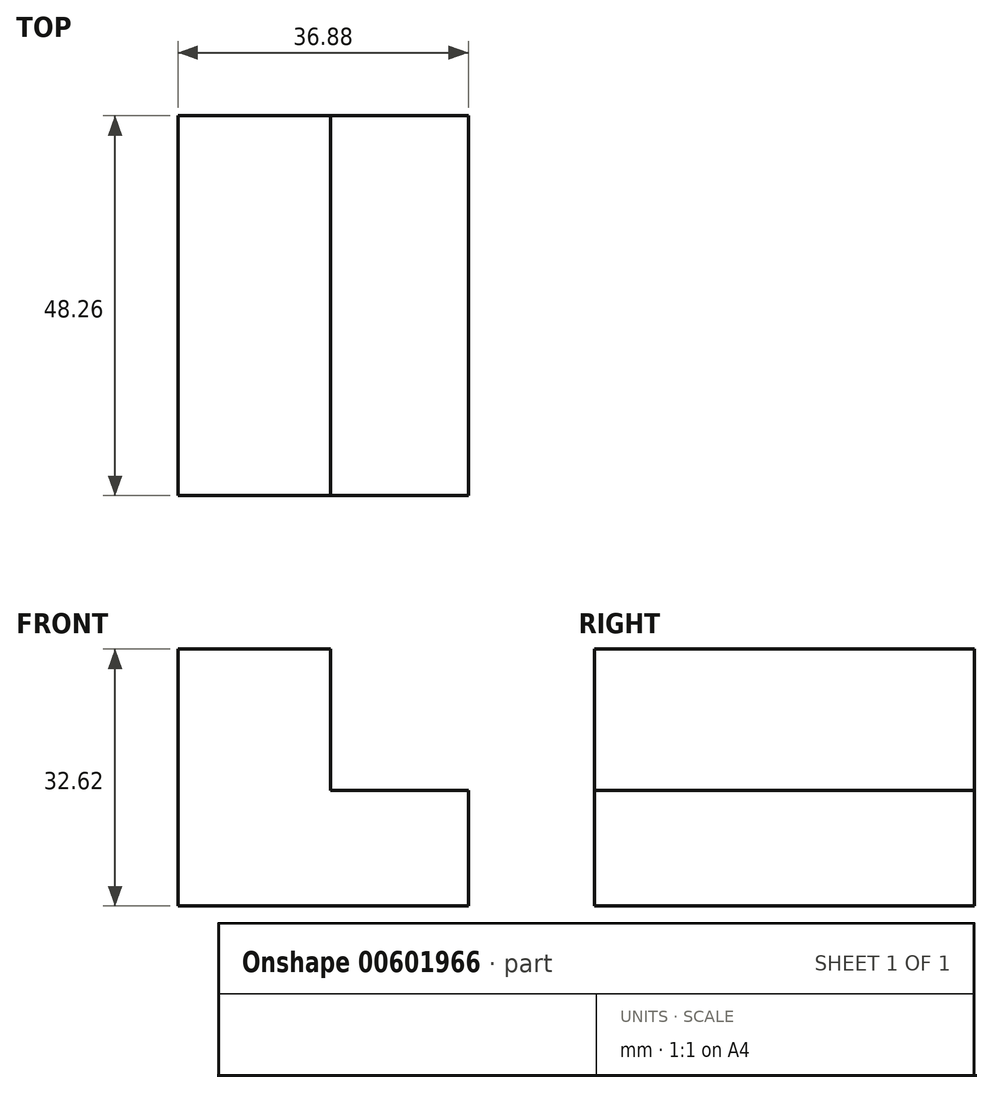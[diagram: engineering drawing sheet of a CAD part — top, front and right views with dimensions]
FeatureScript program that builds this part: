
annotation { "Feature Type Name" : "Feature", "Feature Type Description" : "" }
export const myFeature = defineFeature(function(context is Context, id is Id, definition is map)
    precondition{}
    {
        {
            var Q0;
            Q0=qCreatedBy(makeId("Front.planeOp"),FACE);
            var sketch = newSketch(context, id + "F0", { "sketchPlane" : qUnion([Q0])});
            skLineSegment(sketch, "E0", {"start": v(-19.35, 10.67) * mm, "end": v(-19.35, -21.95) * mm});
            skLineSegment(sketch, "E1", {"start": v(-19.35, -21.95) * mm, "end": v(17.53, -21.95) * mm});
            skLineSegment(sketch, "E2", {"start": v(-19.35, 10.67) * mm, "end": v(0, 10.67) * mm});
            skLineSegment(sketch, "E3", {"start": v(0, 10.67) * mm, "end": v(0, -7.32) * mm});
            skLineSegment(sketch, "E4", {"start": v(0, -7.32) * mm, "end": v(17.53, -7.32) * mm});
            skLineSegment(sketch, "E5", {"start": v(17.53, -7.32) * mm, "end": v(17.53, -21.95) * mm});
            skSolve(sketch);
        }
        {
            var Q0;
            Q0=makeQuery(id+"F0.imprint","IMPRINT",FACE,{"disambiguationData":[TD([[makeQuery(id+"F0.imprint","IMPRINT",EDGE,{"derivedFrom":sQuery(id+"F0.wireOp",EDGE,"E0")}),1.0]])]});
            extrude(context, id + "F1", {"entities" : qUnion([Q0]), "depth" : 48.26 * mm, "offsetDistance" : 25.4 * mm});
        }
    });
